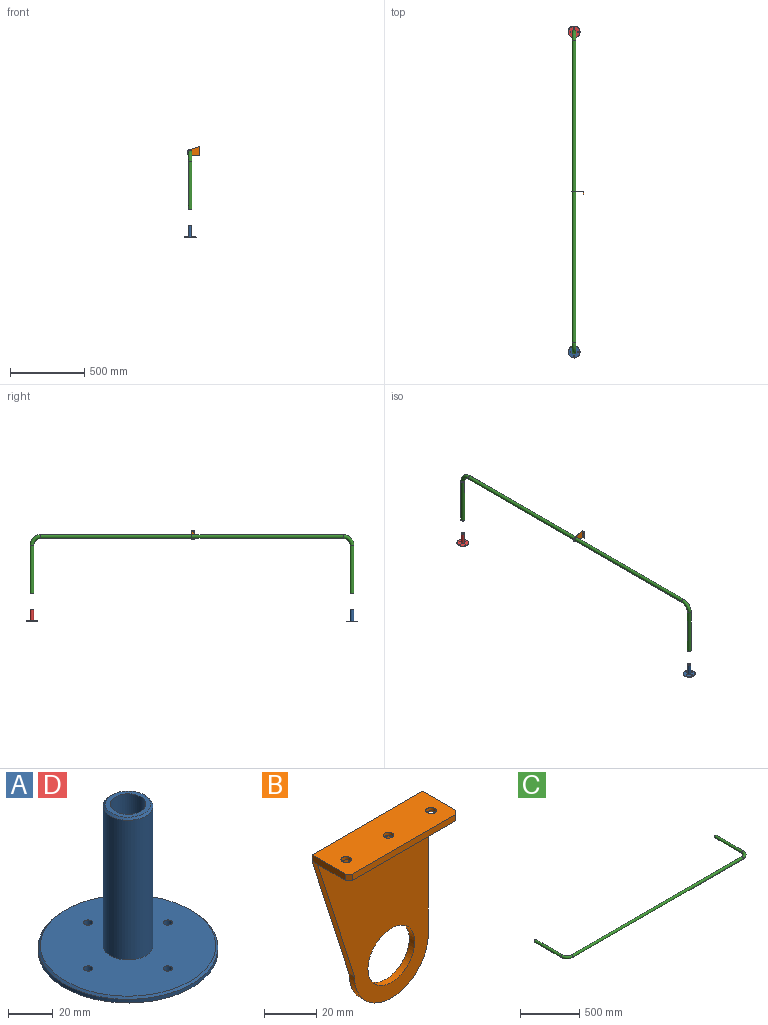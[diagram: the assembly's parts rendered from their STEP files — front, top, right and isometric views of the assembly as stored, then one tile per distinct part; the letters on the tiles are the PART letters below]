
ASSEMBLY  parts=4 mates=3
PART A: 12 faces, bbox 80x80x80 mm
  f0: cylinder r=11.1mm len=76mm, axis (0,0,-1), area 5300.5mm2, adj f9,f10
  f1: cylinder r=7.9mm len=80mm, axis (0,0,-1), area 3971mm2, adj f2,f3
  f2: plane 20.2x20.2mm, normal (0,0,1), area 124.4mm2, adj f1,f10
  f3: plane 80x80mm, normal (0,0,-1), area 4780.2mm2, adj f1,f4,f5,f6,f7,f8
  f4: cylinder r=2mm len=4mm, axis (0,0,-1), area 37.7mm2, adj f3,f9
  f5: cylinder r=2mm len=4mm, axis (0,0,-1), area 37.7mm2, adj f3,f9
  f6: cylinder r=2mm len=4mm, axis (0,0,-1), area 37.7mm2, adj f3,f9
  f7: cylinder r=2mm len=4mm, axis (0,0,-1), area 37.7mm2, adj f3,f9
  f8: cylinder r=40mm len=80mm, axis (0,0,-1), area 502.7mm2, adj f3,f11
  f9: plane 78x78mm, normal (0,0,1), area 4341mm2, adj f0,f4,f5,f6,f7,f11
  f10: cone r=10.1mm half-angle=45deg, axis (0,0,-1), area 94.2mm2, adj f0,f2
  f11: cone r=39mm half-angle=45deg, axis (0,0,-1), area 351mm2, adj f8,f9
PART B: 18 faces, bbox 60x20x85.7 mm
  f0: plane 62.7x20mm, normal (-0.95,0,-0.3), area 197.4mm2, adj f1,f4,f5,f6
  f1: cylinder r=20mm len=40mm, axis (0,1,0), area 188.5mm2, adj f0,f2,f4,f5
  f2: plane 65.7x18mm, normal (1,0,0), area 242.1mm2, adj f1,f4,f5,f11,f12,f16
  f3: cylinder r=12.7mm len=25.4mm, axis (0,1,0), area 239.4mm2, adj f4,f5
  f4: plane 82.7x60mm, normal (0,-1,0), area 3256.6mm2, adj f0,f1,f2,f3,f12
  f5: plane 85.7x60mm, normal (0,1,0), area 3436.6mm2, adj f0,f1,f2,f3,f6,f11
  f6: plane 18x3mm, normal (-1,0,0), area 54mm2, adj f0,f5,f11,f12,f17
  f7: cylinder r=2mm len=4mm, axis (0,0,-1), area 18.8mm2, adj f11,f14
  f8: cylinder r=2mm len=4mm, axis (0,0,-1), area 18.8mm2, adj f11,f15
  f9: plane 56x3mm, normal (0,-1,0), area 168mm2, adj f11,f12,f16,f17
  f10: cylinder r=2mm len=4mm, axis (0,0,-1), area 18.8mm2, adj f11,f13
  f11: plane 60x20mm, normal (0,0,1), area 1158.3mm2, adj f2,f5,f6,f7,f8,f9,f10,f16
  f12: plane 60x17mm, normal (0,0,-1), area 900.5mm2, adj f2,f4,f6,f9,f13,f14,f15,f16
  f13: cone r=3.5mm half-angle=45deg, axis (0,0,-1), area 36.7mm2, adj f10,f12
  f14: cone r=3.5mm half-angle=45deg, axis (0,0,-1), area 36.7mm2, adj f7,f12
  f15: cone r=3.5mm half-angle=45deg, axis (0,0,-1), area 36.7mm2, adj f8,f12
  f16: plane 3x2mm, normal (0.71,-0.71,0), area 8.5mm2, adj f2,f9,f11,f12
  f17: plane 3x2mm, normal (-0.71,-0.71,0), area 8.5mm2, adj f6,f9,f11,f12
PART C: 12 faces, bbox 2187.4x398.7x25.4 mm
  f0: cylinder r=11.1mm len=320mm, axis (0,-1,0), area 22317.9mm2, adj f1,f5
  f1: torus R=60mm, axis (0,0,1), area 6573.2mm2, adj f0,f2
  f2: cylinder r=11.1mm len=2030mm, axis (1,0,0), area 141579mm2, adj f1,f3
  f3: torus R=60mm, axis (0,0,1), area 6573.2mm2, adj f2,f4
  f4: cylinder r=11.1mm len=320mm, axis (0,1,0), area 22317.9mm2, adj f3,f6
  f5: plane 25.4x25.4mm, normal (0,1,0), area 119.6mm2, adj f0,f7
  f6: plane 25.4x25.4mm, normal (0,1,0), area 119.6mm2, adj f4,f11
  f7: cylinder r=12.7mm len=320mm, axis (0,-1,0), area 25534.9mm2, adj f5,f8
  f8: torus R=60mm, axis (0,0,1), area 7520.6mm2, adj f7,f9
  f9: cylinder r=12.7mm len=2030mm, axis (1,0,0), area 161986.8mm2, adj f8,f10
  f10: torus R=60mm, axis (0,0,1), area 7520.6mm2, adj f9,f11
  f11: cylinder r=12.7mm len=320mm, axis (0,1,0), area 25534.9mm2, adj f6,f10
PART D: same geometry as A
PLACE A rot(axis=(0,0,-1),90deg) t=(304.65,-1083.86,-123.03)mm
PLACE B rot(axis=(0,1,0),90deg) t=(304.65,-5.86,447.97)mm
PLACE C rot(axis=(-0.58,0.58,-0.58),120deg) t=(304.65,-8.86,447.97)mm
PLACE D rot(axis=(0,0,-1),90deg) t=(304.65,1066.14,-122.11)mm
MATE cylindrical C.f9 <-> B.f3  axis (0,-1,0) through (304.65,-8.86,447.97)mm
MATE slider C.f11 <-> A.f0  axis (0,0,-1) through (304.65,-1083.86,67.97)mm
MATE slider C.f7 <-> D.f0  axis (0,0,1) through (304.65,1066.14,67.97)mm
